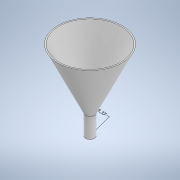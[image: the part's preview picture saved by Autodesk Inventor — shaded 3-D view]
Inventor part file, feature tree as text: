
AUTODESK INVENTOR PART (.ipt)
format: ipt  version: 2020.2 (Build 242310000, 310)  size: 125,440 bytes
history: native  units: in
note: dims shown in document units (in); Inventor stores cm internally (conversion verified against a paired STEP export)
features: other x2, revolve x1, sketch x1
ambient origin geometry x8: Origin, YZ Plane, XZ Plane, XY Plane, X Axis, Y Axis, Z Axis, Center Point
bodies: Solid1 (feature_tree)
feature tree (4):
  other  "Annotations"
  revolve  "Revolution1"  [1 undecoded]
  sketch  "Sketch1"  dims[d0=0.0625in d1=0.225in d2=1.0in d3=4.0in d4=1.625in d6=90.0deg d7=3.0in d10=1.712in d11=0.325in]
  other  "Diameter Dimension 1"
note: 1 required parameter value undecoded (feature->parameter linkage not recoverable at this tier; creation-order binding heuristic only, values carry confidence <= 0.55)
